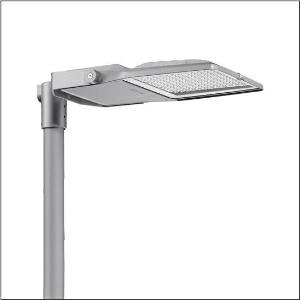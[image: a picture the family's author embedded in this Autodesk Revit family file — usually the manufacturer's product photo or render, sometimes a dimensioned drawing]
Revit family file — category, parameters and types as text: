
# Revit family: floodlight_fl_21_midi___pl52_5xa7786f2d3a_9b56
name_source: partatom
category: Lighting Fixtures
units: mm (PartAtom-declared; Revit-internal decimal feet)

## family parameters
Cut with Voids When Loaded = No
Host = Face
Light Source = No
Part Type = Normal
Room Calculation Point = No
Round Connector Dimension = Use Diameter
Shared = No

## types (1)
- --- (1 x LED, 35750 lm, 271.6 W, 3000K)
    Apparent Load = 272 VA
    CIE Flux Codes = 26 60 98 100 100
    Color Rendering = 70
    Color Temperature = 3000K
    Default Elevation = 1800 mm
    Description = Floodlight FL 21 midi, floodlight, primary light control with lens, of PMMA, primary optical cover: protective disc, of toughened safety glass, transparent, light distribution: PL52, light emission: direct distribution, installation type: surface-mounted, LED, High Power LED, rated luminous flux: 35.750lm, luminous efficacy: 132lm/W, light colour: 730, colour temperature: 3000K, control gear: ECG Smart Interface, control: flexible luminous flux parameterisation, time-dependent luminous flux control, constant luminous flux control, overheat protection, pre-setting: logarithmic dimming characteristic, with terminal, 6-pole, mains connection: 220..240V, AC, 50/60Hz, start of lifetime: 272W, end of service life: 287W, reduction: 123W, luminaire housing, of diecast aluminium, powder-coated, Siteco® metallic grey (DB 702S), corrosivity category C5 mid according to DIN EN ISO 12944, sealing non-destructively replaceable, please order mast flange separately, mast bracket, of steel, galvanised, powder-coated, Siteco® metallic grey (DB 702S), Smart Interface below and above, protection rating (complete): IP66, insulation class (complete): insulation class II (safety insulation), certification: CE, ENEC, VDE, protection symbol: D, impact resistance: IK08, permissible operating ambient temperature: -40..+40°C, permissible operating ambient temperature for outdoor applications: -40..+50°C, standard: DIN EN 12944, LABS conformity tested according to VDMA 24364:2018-05, packaging unit: 1 piece

Light Distribution: PL52
    Height = 76 mm
    Lamp = 1 x LED
    Lamp Light Flux = 35750 lm
    Lamp Power = 271.6 W
    Lamp count = 1
    Length = 657 mm
    Luminous efficacy = 132 lm/W
    Manufacturer = Siteco
    ModVariant = No
    Model = 5XA7786F2D3A
    Number of Poles = 1
    OnlyDefault = Yes
    Power Factor = 1
    Product Name = Floodlight FL 21 midi | PL52
    Product group = floodlight | pylon annexe
    ProductGroupID = 6200
    Protection Class = Protection class II
    Protection Degree = IP 66
    RLX_Detail_Level = 1
    RLX_Emergency_Light_Flux = 0 lm
    RLX_Emergency_Type = 0
    RLX_Emergency_Type_DB = No
    RlxData = <blob elided: 153561 chars, md5=2833e320>
    Socket = socket
    Standby Power = 0 W
    System Light Flux = 35750 lm
    System Power = 272 W
    Type Comments = factory setting: luminous flux: 100 % | dim-lin: 254 | 620 mA
    Type Image = l_1007123.jpg
    URL = http://relux.com
    VarID = @adj_148687
    Voltage = 0 V
    Weight = 0.00 kg
    Width = 442 mm

## geometry (parser evidence)
native form markers: Blend x4, Sweep x12
no freeform markers — native parametric forms only
